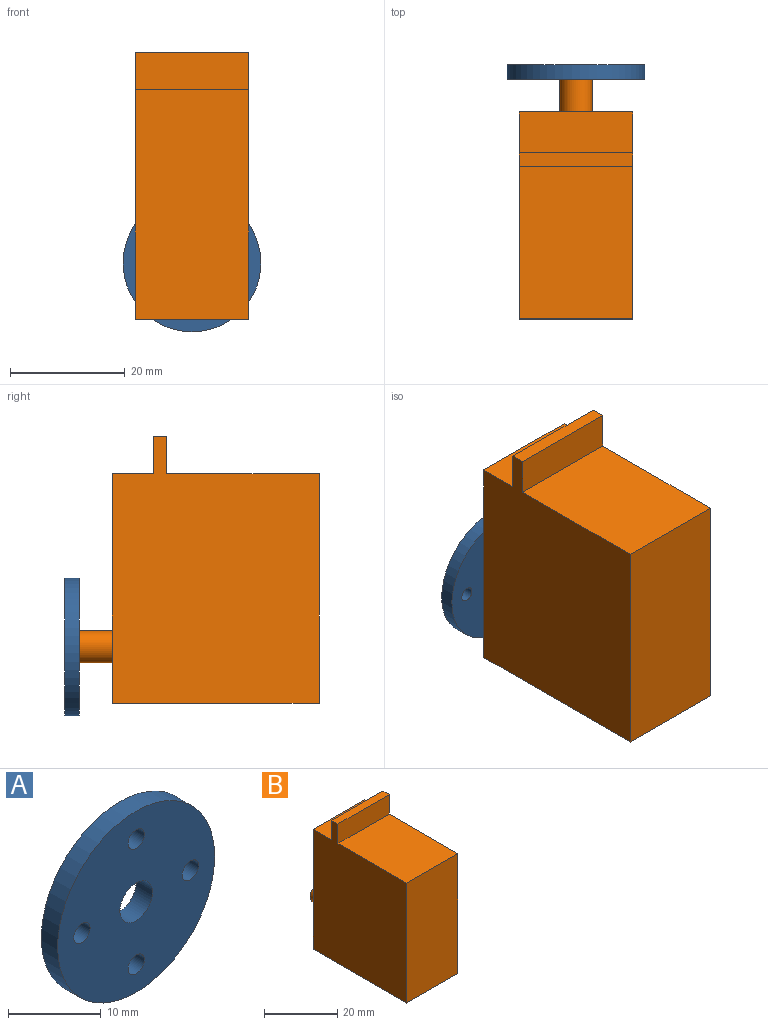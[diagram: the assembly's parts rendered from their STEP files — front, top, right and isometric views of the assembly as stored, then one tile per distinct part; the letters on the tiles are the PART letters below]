
ASSEMBLY  parts=2 mates=1
PART A: 8 faces, bbox 24x2.5x24 mm
  f0: plane 24x24mm, normal (0,1,0), area 413.1mm2, adj f2,f3,f4,f5,f6,f7
  f1: plane 24x24mm, normal (0,-1,0), area 413.1mm2, adj f2,f3,f4,f5,f6,f7
  f2: cylinder r=12mm len=24mm, axis (0,-1,0), area 188.5mm2, adj f0,f1
  f3: cylinder r=2.5mm len=5mm, axis (0,-1,0), area 39.3mm2, adj f0,f1
  f4: cylinder r=1.25mm len=2.5mm, axis (0,-1,0), area 19.6mm2, adj f0,f1
  f5: cylinder r=1.25mm len=2.5mm, axis (0,-1,0), area 19.6mm2, adj f0,f1
  f6: cylinder r=1.25mm len=2.5mm, axis (0,-1,0), area 19.6mm2, adj f0,f1
  f7: cylinder r=1.25mm len=2.5mm, axis (0,-1,0), area 19.6mm2, adj f0,f1
PART B: 12 faces, bbox 19.7x44.3x46.5 mm
  f0: plane 19.7x7.14mm, normal (0,0,1), area 140.7mm2, adj f2,f3,f5,f8
  f1: plane 26.5x19.7mm, normal (0,0,1), area 522mm2, adj f2,f3,f6,f7
  f2: plane 46.5x36mm, normal (-1,0,0), area 1455.3mm2, adj f0,f1,f4,f5,f6,f7,f8,f9
  f3: plane 46.5x36mm, normal (1,0,0), area 1455.3mm2, adj f0,f1,f4,f5,f6,f7,f8,f9
  f4: plane 36x19.7mm, normal (0,0,-1), area 709.2mm2, adj f2,f3,f5,f6
  f5: plane 40x19.7mm, normal (0,1,0), area 763mm2, adj f0,f2,f3,f4,f10
  f6: plane 40x19.7mm, normal (0,-1,0), area 788mm2, adj f1,f2,f3,f4
  f7: plane 19.7x6.5mm, normal (0,-1,0), area 128mm2, adj f1,f2,f3,f9
  f8: plane 19.7x6.5mm, normal (0,1,0), area 128mm2, adj f0,f2,f3,f9
  f9: plane 19.7x2.36mm, normal (0,0,1), area 46.5mm2, adj f2,f3,f7,f8
  f10: cylinder r=2.82mm len=8.25mm, axis (0,-1,0), area 146.1mm2, adj f5,f11
  f11: plane 5.64x5.64mm, normal (0,1,0), area 25mm2, adj f10
PLACE A rot(axis=(1,0,0),180deg) t=(0,44.25,-10.18)mm
PLACE B at identity
MATE revolute A.f2 <-> B.f10  axis (0,1,0) through (0,44.25,-10.18)mm
